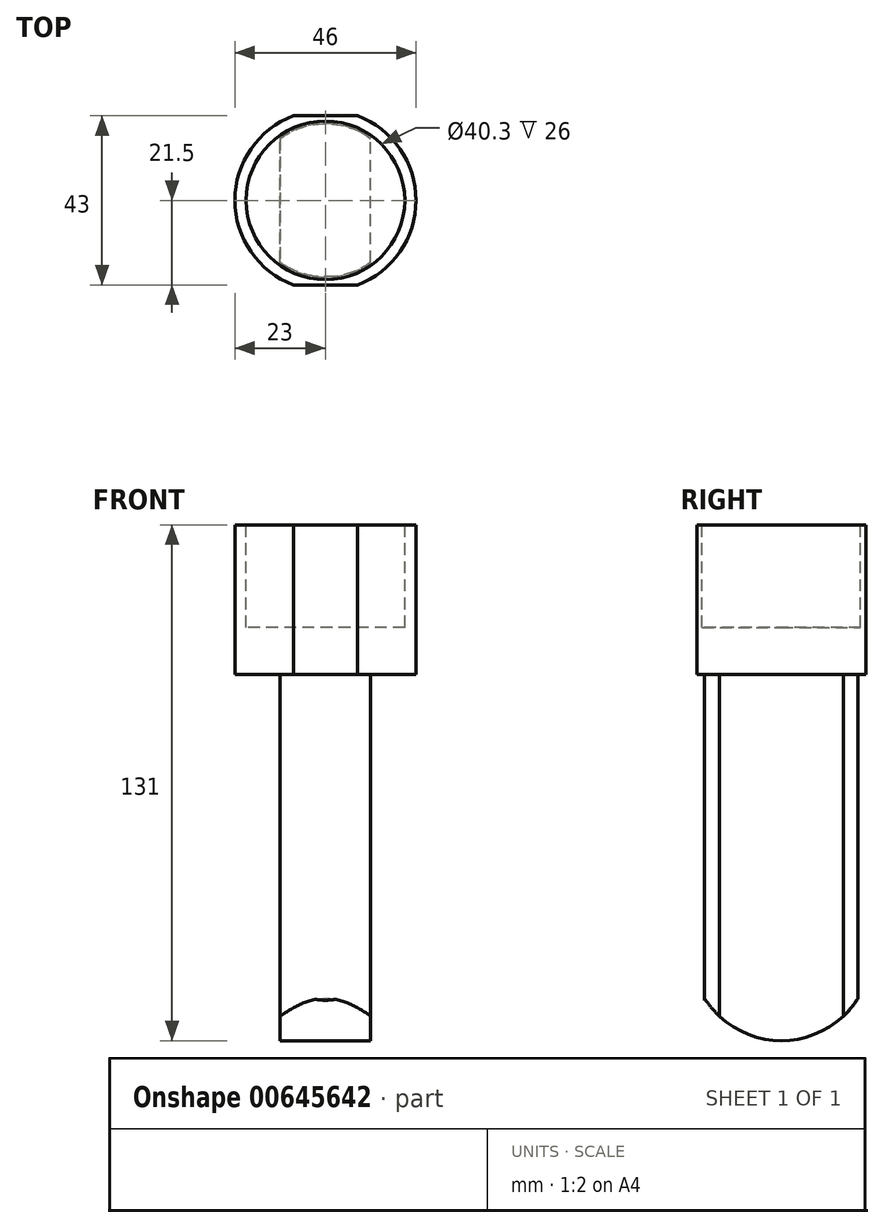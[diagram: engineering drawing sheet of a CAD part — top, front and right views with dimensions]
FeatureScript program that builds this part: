
annotation { "Feature Type Name" : "Feature", "Feature Type Description" : "" }
export const myFeature = defineFeature(function(context is Context, id is Id, definition is map)
    precondition{}
    {
        {
            var Q0;
            Q0=qCreatedBy(makeId("Top.planeOp"),FACE);
            var sketch = newSketch(context, id + "F0", { "sketchPlane" : qUnion([Q0])});
            skArc(sketch, "E0", {"start": v(-8.17, 21.5) * mm, "mid": v(-23, 0) * mm, "end": v(-8.17, -21.5) * mm});
            skLineSegment(sketch, "E1", {"start": v(-8.17, 21.5) * mm, "end": v(8.17, 21.5) * mm});
            skLineSegment(sketch, "E2", {"start": v(-8.17, -21.5) * mm, "end": v(8.17, -21.5) * mm});
            skArc(sketch, "E3.trimOffspring", {"start": v(8.17, -21.5) * mm, "mid": v(23, 0) * mm, "end": v(8.17, 21.5) * mm});
            skSolve(sketch);
        }
        {
            var Q0;
            Q0=makeQuery(id+"F0.imprint","IMPRINT",FACE,{"disambiguationData":[TD([[makeQuery(id+"F0.imprint","IMPRINT",EDGE,{"derivedFrom":sQuery(id+"F0.wireOp",EDGE,"E0")}),1.0]])]});
            extrude(context, id + "F1", {"entities" : qUnion([Q0]), "depth" : 38 * mm, "offsetDistance" : 25 * mm});
        }
        {
            var Q0;
            Q0=makeQuery(id+"F1.opExtrude","CAP_FACE",FACE,{"disambiguationData":[OSD([sQuery(id+"F0.wireOp",EDGE,"E0"),sQuery(id+"F0.wireOp",EDGE,"E1"),sQuery(id+"F0.wireOp",EDGE,"E2"),sQuery(id+"F0.wireOp",EDGE,"E3.trimOffspring")])],"isStart":false});
            var sketch = newSketch(context, id + "F2", { "sketchPlane" : qUnion([Q0])});
            skCircle(sketch, "E4", {"center": v(0, 0) * mm, "radius": 20.15 * mm});
            skSolve(sketch);
        }
        {
            var Q0;
            Q0=makeQuery(id+"F2.imprint","IMPRINT",FACE,{"disambiguationData":[TD([[makeQuery(id+"F2.imprint","IMPRINT",EDGE,{"derivedFrom":sQuery(id+"F2.wireOp",EDGE,"E4")}),1.0]])]});
            extrude(context, id + "F3", {"entities" : qUnion([Q0]), "operationType" : NewBodyOperationType.REMOVE, "oppositeDirection" : true, "depth" : 26 * mm, "offsetDistance" : 25 * mm});
        }
        {
            var Q0;
            Q0=makeQuery(id+"F1.opExtrude","CAP_FACE",FACE,{"disambiguationData":[OSD([sQuery(id+"F0.wireOp",EDGE,"E0"),sQuery(id+"F0.wireOp",EDGE,"E1"),sQuery(id+"F0.wireOp",EDGE,"E2"),sQuery(id+"F0.wireOp",EDGE,"E3.trimOffspring")])],"isStart":true});
            var sketch = newSketch(context, id + "F4", { "sketchPlane" : qUnion([Q0])});
            skArc(sketch, "E5", {"start": v(-11.5, -15.75) * mm, "mid": v(0, -19.5) * mm, "end": v(11.5, -15.75) * mm});
            skLineSegment(sketch, "E6", {"start": v(-11.5, 15.75) * mm, "end": v(-11.5, -15.75) * mm});
            skLineSegment(sketch, "E7.MirrorCS", {"start": v(11.5, 15.75) * mm, "end": v(11.5, -15.75) * mm});
            skArc(sketch, "E8.trimOffspring", {"start": v(11.5, 15.75) * mm, "mid": v(0, 19.5) * mm, "end": v(-11.5, 15.75) * mm});
            skSolve(sketch);
        }
        {
            var Q0;
            Q0 = qSketchRegion(id + "F4", true);
            var Q1;
            Q1=makeQuery(id+"F4.imprint","IMPRINT",FACE,{"disambiguationData":[TD([[makeQuery(id+"F4.imprint","IMPRINT",EDGE,{"derivedFrom":sQuery(id+"F4.wireOp",EDGE,"E5")}),1.0]])]});
            extrude(context, id + "F5", {"entities" : qUnion([Q0, Q1]), "operationType" : NewBodyOperationType.ADD, "depth" : 93 * mm, "offsetDistance" : 25 * mm});
        }
        {
            var Q0;
            Q0=makeQuery(id+"F5.opExtrude","SWEPT_FACE",FACE,{"disambiguationData":[OSD([sQuery(id+"F4.wireOp",EDGE,"E6")])]});
            var sketch = newSketch(context, id + "F6", { "sketchPlane" : qUnion([Q0])});
            skCircle(sketch, "E9", {"center": v(0, -70) * mm, "radius": 23 * mm});
            skLineSegment(sketch, "E10", {"start": v(-19.6, -82.04) * mm, "end": v(-36.66, -104.73) * mm});
            skLineSegment(sketch, "E11", {"start": v(-36.66, -104.73) * mm, "end": v(37.7, -105.3) * mm});
            skLineSegment(sketch, "E12", {"start": v(37.7, -105.3) * mm, "end": v(19.32, -82.48) * mm});
            skSolve(sketch);
        }
        {
            var Q0;
            {var subQ5=sQuery(id+"F6.wireOp",EDGE,"E10");Q0=makeQuery(id+"F6.imprint","IMPRINT",FACE,{"disambiguationData":[TD([[makeQuery(id+"F6.imprint","IMPRINT",EDGE,{"derivedFrom":subQ5}),1.0]])]});}
            var Q1;
            {var subQ0=sQuery(id+"F6.wireOp",EDGE,"E9");var subQ1=sQuery(id+"F4.wireOp",EDGE,"E6");var subQ4=makeQuery(id+"F5.opExtrude","CAP_EDGE",EDGE,{"disambiguationData":[OSD([subQ1])],"isStart":false});var subQ5=makeQuery(id+"F6.imprint","INTERSECT",VERTEX,{"derivedFrom":[subQ4,subQ0]});Q1=makeQuery(id+"F6.imprint","IMPRINT",FACE,{"disambiguationData":[TD([[makeQuery(id+"F6.imprint","IMPRINT",EDGE,{"disambiguationData":[TD([[subQ5,1.0]])],"derivedFrom":subQ0}),-1.0]])]});}
            var Q2;
            {var subQ0=sQuery(id+"F6.wireOp",EDGE,"E9");var subQ1=sQuery(id+"F4.wireOp",EDGE,"E6");var subQ2=makeQuery(id+"F5.opExtrude","CAP_EDGE",EDGE,{"disambiguationData":[OSD([subQ1])],"isStart":false});var subQ3=makeQuery(id+"F6.imprint","INTERSECT",VERTEX,{"derivedFrom":[subQ2,subQ0]});Q2=makeQuery(id+"F6.imprint","IMPRINT",FACE,{"disambiguationData":[TD([[makeQuery(id+"F6.imprint","IMPRINT",EDGE,{"disambiguationData":[TD([[subQ3,-1.0]])],"derivedFrom":subQ0}),-1.0]])]});}
            extrude(context, id + "F7", {"entities" : qUnion([Q0, Q1, Q2]), "operationType" : NewBodyOperationType.REMOVE, "endBound" : BoundingType.THROUGH_ALL, "oppositeDirection" : true, "depth" : 25 * mm, "offsetDistance" : 25 * mm});
        }
    });
